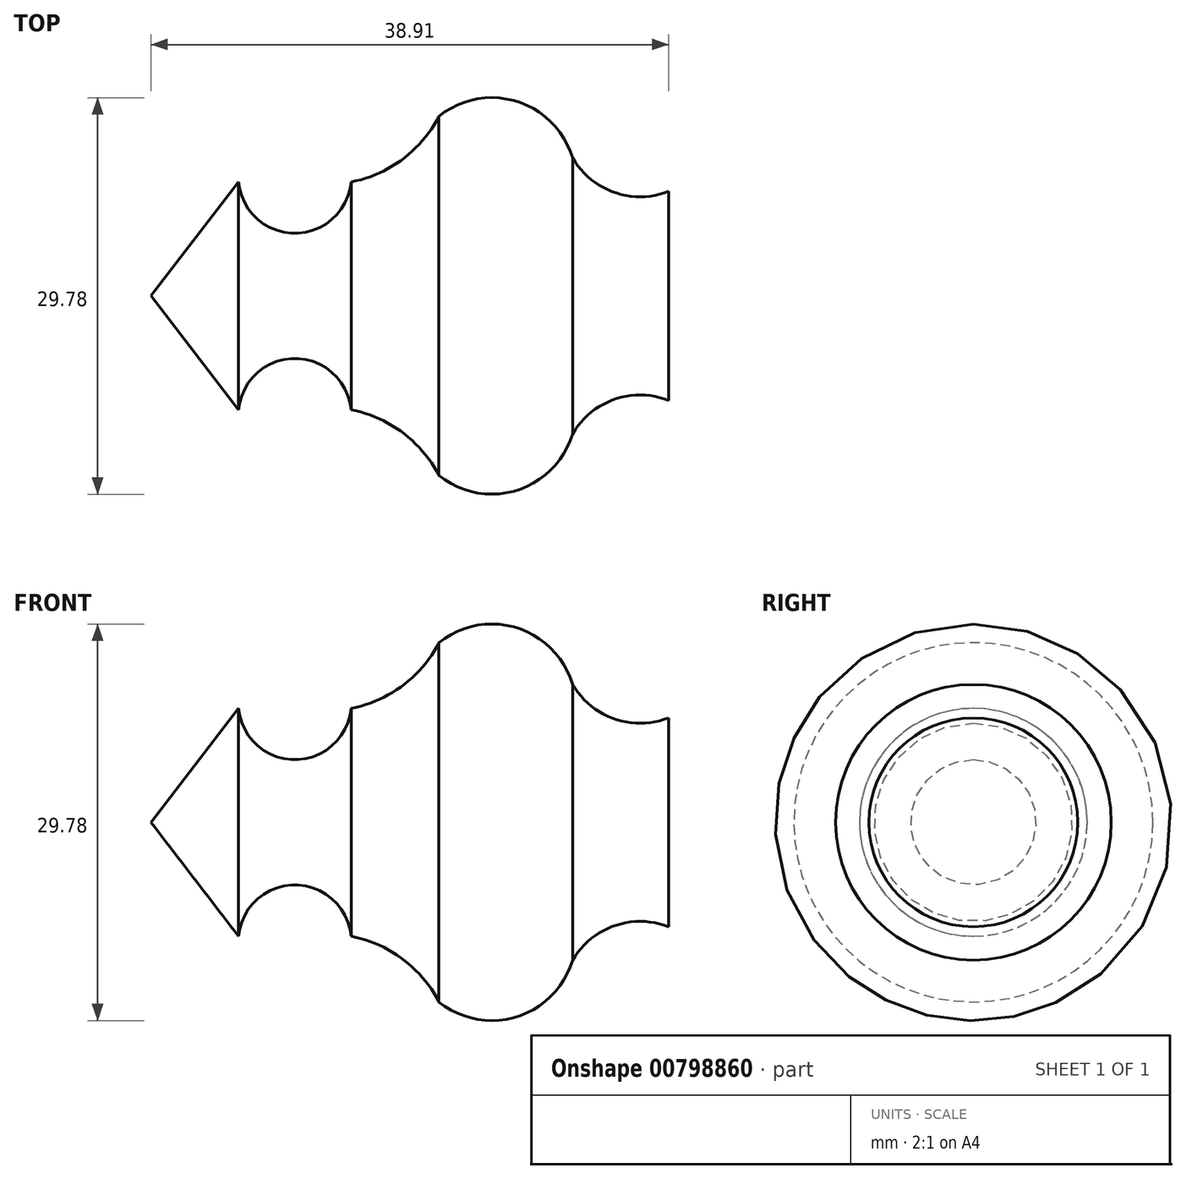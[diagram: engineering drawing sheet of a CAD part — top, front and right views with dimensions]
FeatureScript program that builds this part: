
annotation { "Feature Type Name" : "Feature", "Feature Type Description" : "" }
export const myFeature = defineFeature(function(context is Context, id is Id, definition is map)
    precondition{}
    {
        {
            var Q0;
            Q0=qCreatedBy(makeId("Top.planeOp"),FACE);
            var sketch = newSketch(context, id + "F0", { "sketchPlane" : qUnion([Q0])});
            skLineSegment(sketch, "E0", {"start": v(-26.12, 16.4) * mm, "end": v(12.79, 16.4) * mm});
            skLineSegment(sketch, "E1", {"start": v(12.79, 16.4) * mm, "end": v(12.79, 24.24) * mm});
            skArc(sketch, "E2", {"start": v(5.57, 26.75) * mm, "mid": v(8.72, 24.17) * mm, "end": v(12.79, 24.24) * mm});
            skArc(sketch, "E3", {"start": v(5.57, 26.75) * mm, "mid": v(1.39, 31) * mm, "end": v(-4.47, 29.89) * mm});
            skArc(sketch, "E4", {"start": v(-11.06, 24.95) * mm, "mid": v(-7.2, 26.66) * mm, "end": v(-4.47, 29.89) * mm});
            skArc(sketch, "E5", {"start": v(-19.53, 24.95) * mm, "mid": v(-15.3, 21.1) * mm, "end": v(-11.06, 24.95) * mm});
            skLineSegment(sketch, "E6", {"start": v(-19.53, 24.95) * mm, "end": v(-26.12, 16.4) * mm});
            skSolve(sketch);
        }
        {
            var Q0;
            Q0 = qSketchRegion(id + "F0", true);
            var Q1;
            Q1=sQuery(id+"F0.wireOp",EDGE,"E0");
            revolve(context, id + "F1", {"surfaceOperationType" : NewSurfaceOperationType.NEW, "entities" : qUnion([Q0]), "axis" : qUnion([Q1]), "revolveType" : RevolveType.FULL});
        }
    });
